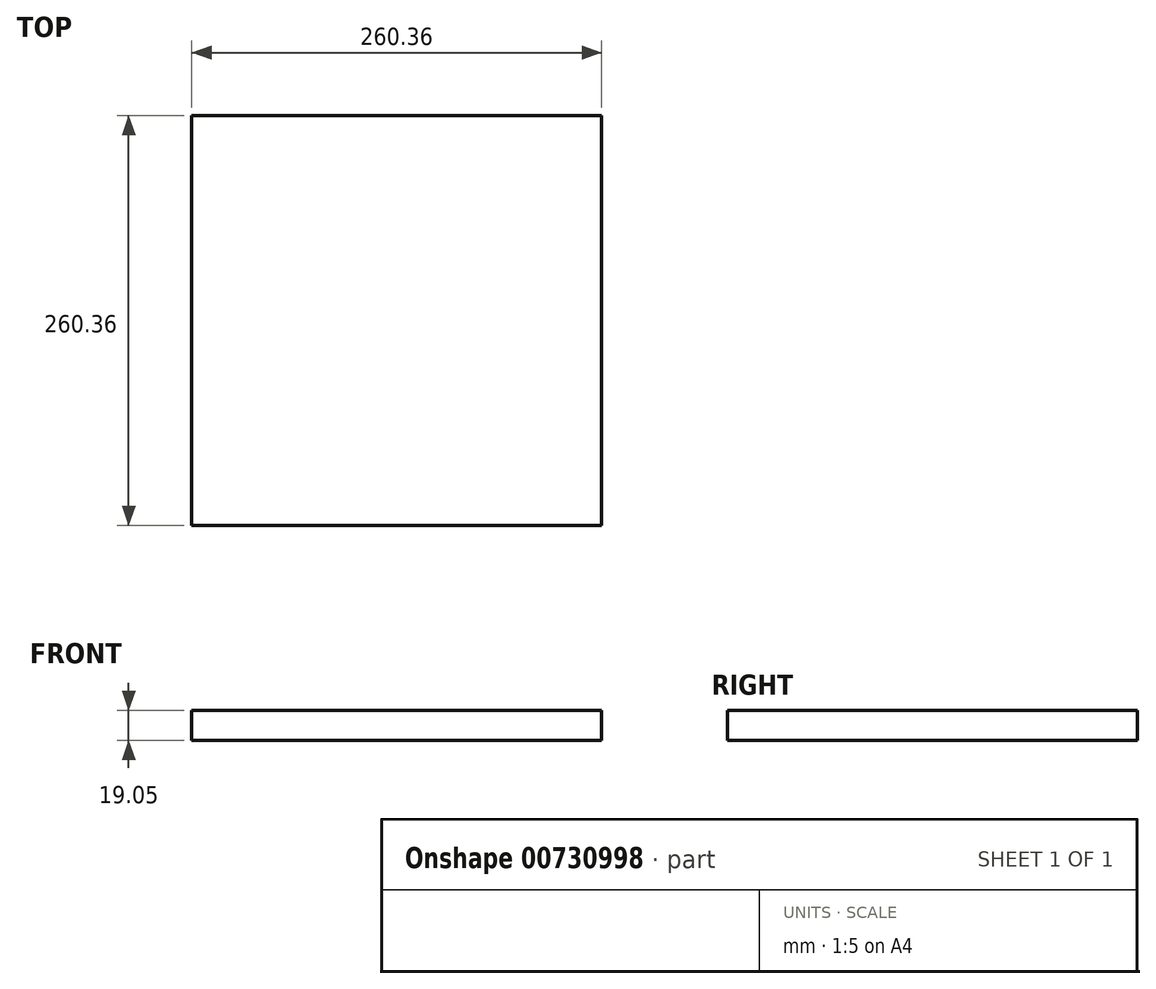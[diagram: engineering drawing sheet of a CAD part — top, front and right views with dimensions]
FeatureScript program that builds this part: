
annotation { "Feature Type Name" : "Feature", "Feature Type Description" : "" }
export const myFeature = defineFeature(function(context is Context, id is Id, definition is map)
    precondition{}
    {
        {
            var Q0;
            Q0=qCreatedBy(makeId("Top.planeOp"),FACE);
            var sketch = newSketch(context, id + "F0", { "sketchPlane" : qUnion([Q0])});
            skLineSegment(sketch, "E0.bottom", {"start": v(130.18, -130.17) * mm, "end": v(-130.18, -130.18) * mm});
            skLineSegment(sketch, "E0.top", {"start": v(130.18, 130.18) * mm, "end": v(-130.18, 130.17) * mm});
            skLineSegment(sketch, "E0.left", {"start": v(130.18, -130.17) * mm, "end": v(130.18, 130.18) * mm});
            skLineSegment(sketch, "E0.right", {"start": v(-130.18, -130.18) * mm, "end": v(-130.18, 130.17) * mm});
            skPoint(sketch, "E0.middle", {"position": v(0, 0) * mm});
            skSolve(sketch);
        }
        {
            var Q0;
            Q0=makeQuery(id+"F0.imprint","IMPRINT",FACE,{"disambiguationData":[TD([[makeQuery(id+"F0.imprint","IMPRINT",EDGE,{"derivedFrom":sQuery(id+"F0.wireOp",EDGE,"E0.bottom")}),-1.0]])]});
            extrude(context, id + "F1", {"entities" : qUnion([Q0]), "depth" : 19.05 * mm, "offsetDistance" : 25.4 * mm});
        }
    });
